annotation { "Feature Type Name" : "Feature", "Feature Type Description" : "" }
export const myFeature = defineFeature(function(context is Context, id is Id, definition is map)
    precondition{}
    {
        {
            var Q0;
            Q0=qCreatedBy(makeId("Front.planeOp"),FACE);
            var sketch = newSketch(context, id + "F0", { "sketchPlane" : qUnion([Q0])});
            skLineSegment(sketch, "E0", {"start": v(3.41, -76.2) * mm, "end": v(74.41, -76.2) * mm});
            skLineSegment(sketch, "E1", {"start": v(3.41, -76.2) * mm, "end": v(-67.59, -76.2) * mm});
            skLineSegment(sketch, "E2", {"start": v(3.41, -76.2) * mm, "end": v(3.41, 93.8) * mm, "construction": true});
            skLineSegment(sketch, "E3", {"start": v(-69.59, -74.2) * mm, "end": v(-69.59, -68.8) * mm});
            skArc(sketch, "E4", {"start": v(-69.59, -74.2) * mm, "mid": v(-69, -75.62) * mm, "end": v(-67.59, -76.2) * mm});
            skArc(sketch, "E5", {"start": v(-67.31, -65.89) * mm, "mid": v(-68.95, -66.95) * mm, "end": v(-69.59, -68.8) * mm});
            skLineSegment(sketch, "E6", {"start": v(76.41, -74.2) * mm, "end": v(76.41, -68.8) * mm});
            skArc(sketch, "E7", {"start": v(74.41, -76.2) * mm, "mid": v(75.83, -75.62) * mm, "end": v(76.41, -74.2) * mm});
            skArc(sketch, "E8", {"start": v(76.41, -68.8) * mm, "mid": v(75.78, -66.95) * mm, "end": v(74.14, -65.89) * mm});
            skLineSegment(sketch, "E9", {"start": v(3.41, 93.8) * mm, "end": v(-20.64, 93.8) * mm});
            skLineSegment(sketch, "E10", {"start": v(-32.34, 78.63) * mm, "end": v(-33.03, 64.93) * mm});
            skLineSegment(sketch, "E11.bottom", {"start": v(-20.64, 93.8) * mm, "end": v(-15.59, 93.8) * mm});
            skArc(sketch, "E12", {"start": v(-20.64, 93.8) * mm, "mid": v(-28.87, 88.05) * mm, "end": v(-32.34, 78.63) * mm});
            skLineSegment(sketch, "E13", {"start": v(-16.64, 49.8) * mm, "end": v(-23.8, 51.6) * mm});
            skLineSegment(sketch, "E14", {"start": v(-33.03, 64.93) * mm, "end": v(-33.15, 62.59) * mm});
            skFitSpline(sketch, "E15", {"points": [v(-33.03, 64.93) * mm, v(-31.85, 55.5) * mm, v(-23.8, 51.6) * mm], "startDerivative": vector(-1.23, -21.29) * mm, "endDerivative": vector(19.8, -5.3) * mm});
            skArc(sketch, "E16", {"start": v(-31.3, -56.88) * mm, "mid": v(-22.49, -52.1) * mm, "end": v(-17.11, -43.63) * mm});
            skLineSegment(sketch, "E17.trimOffspring", {"start": v(-31.3, -56.88) * mm, "end": v(-67.31, -65.89) * mm});
            skPoint(sketch, "E18.orphan", {"position": v(-17.07, -43.5) * mm});
            skPoint(sketch, "E19.end.orphan", {"position": v(-17.07, -43.63) * mm});
            skFitSpline(sketch, "E20", {"points": [v(-17.11, -43.63) * mm, v(-13.44, -10.74) * mm, v(-13.2, 12.32) * mm, v(-14.6, 33.9) * mm, v(-16.23, 47.1) * mm, v(-16.64, 49.8) * mm], "startDerivative": vector(15, 122.65) * mm, "endDerivative": vector(-2.95, 27.62) * mm});
            skLineSegment(sketch, "E21.MirrorCS", {"start": v(3.41, 93.8) * mm, "end": v(27.47, 93.8) * mm});
            skArc(sketch, "E22.MirrorCS", {"start": v(27.47, 93.8) * mm, "mid": v(35.7, 88.05) * mm, "end": v(39.17, 78.63) * mm});
            skLineSegment(sketch, "E23.MirrorCS", {"start": v(39.17, 78.63) * mm, "end": v(39.86, 64.93) * mm});
            skFitSpline(sketch, "E24.MirrorCS", {"points": [v(39.86, 64.93) * mm, v(38.67, 55.5) * mm, v(30.63, 51.6) * mm], "startDerivative": vector(1.23, -21.29) * mm, "endDerivative": vector(-19.8, -5.3) * mm});
            skLineSegment(sketch, "E25.MirrorCS", {"start": v(23.46, 49.8) * mm, "end": v(30.63, 51.6) * mm});
            skFitSpline(sketch, "E26.MirrorCS", {"points": [v(23.94, -43.63) * mm, v(20.27, -10.74) * mm, v(20.04, 12.32) * mm, v(21.43, 33.9) * mm, v(23.06, 47.1) * mm, v(23.46, 49.8) * mm], "startDerivative": vector(-15, 122.65) * mm, "endDerivative": vector(2.95, 27.62) * mm});
            skArc(sketch, "E27.MirrorCS", {"start": v(38.12, -56.88) * mm, "mid": v(29.32, -52.1) * mm, "end": v(23.94, -43.63) * mm});
            skLineSegment(sketch, "E28.MirrorCS", {"start": v(38.12, -56.88) * mm, "end": v(74.14, -65.89) * mm});
            skLineSegment(sketch, "E29", {"start": v(-399996.59, -19.54) * mm, "end": v(-399996.59, 58.62) * mm});
            skSolve(sketch);
        }
        {
            var Q0;
            Q0=makeQuery(id+"F0.imprint","IMPRINT",FACE,{"disambiguationData":[TD([[makeQuery(id+"F0.imprint","IMPRINT",EDGE,{"derivedFrom":sQuery(id+"F0.wireOp",EDGE,"E0")}),1.0]])]});
            var Q1;
            Q1=sQuery(id+"F0.wireOp",EDGE,"E29");
            revolve(context, id + "F1", {"entities" : qUnion([Q0]), "axis" : qUnion([Q1]), "revolveType" : RevolveType.ONE_DIRECTION, "angle" : 60 * degree});
        }
    });